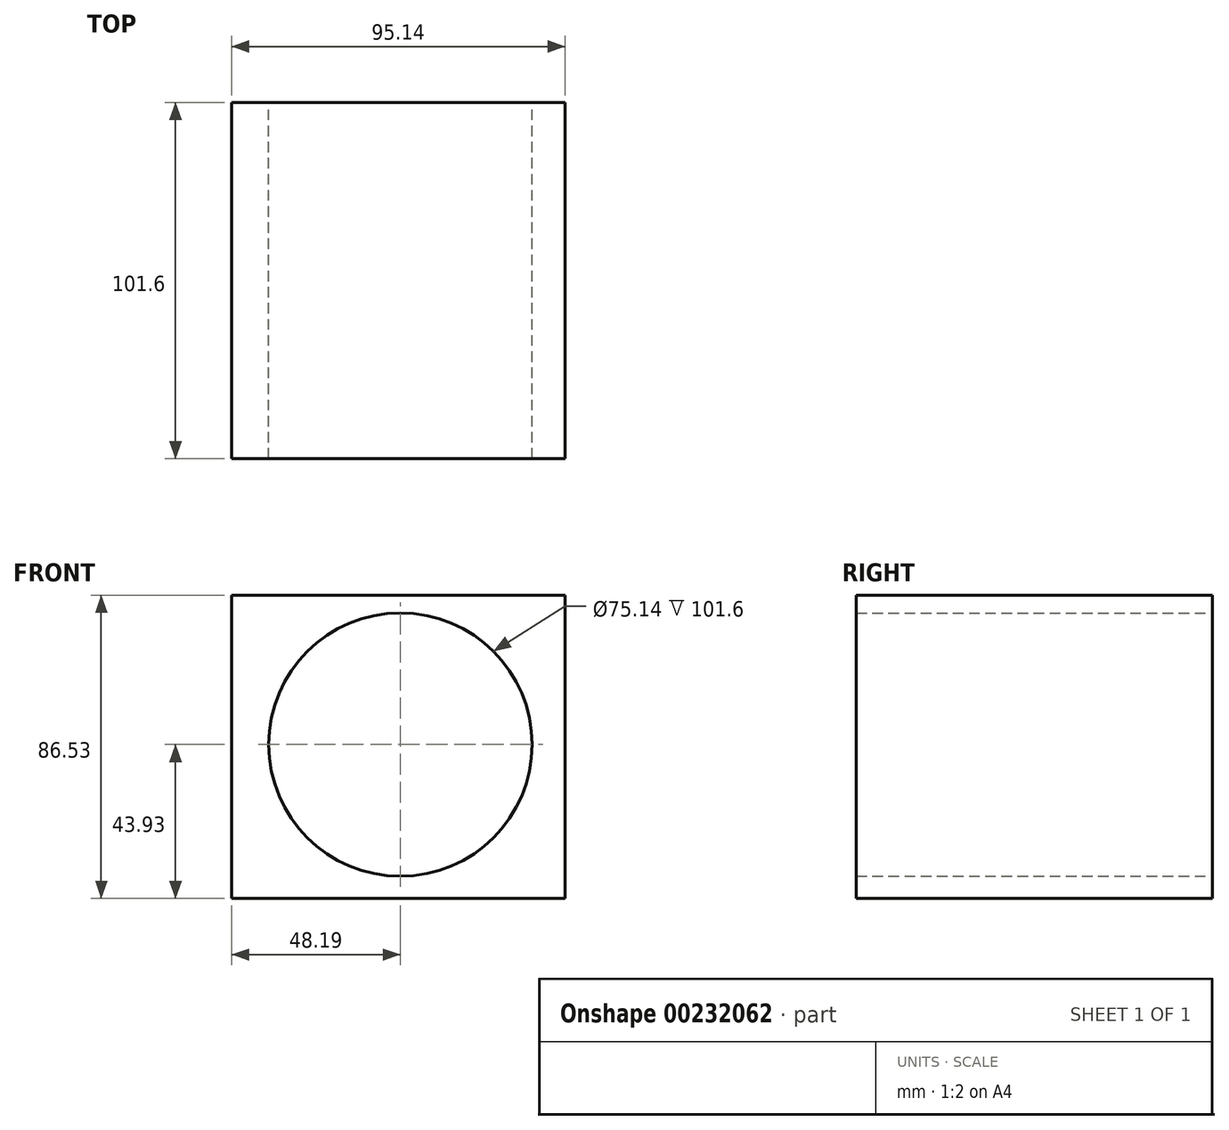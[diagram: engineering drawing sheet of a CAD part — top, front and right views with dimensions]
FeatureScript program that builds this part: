
annotation { "Feature Type Name" : "Feature", "Feature Type Description" : "" }
export const myFeature = defineFeature(function(context is Context, id is Id, definition is map)
    precondition{}
    {
        {
            var Q0;
            Q0=qCreatedBy(makeId("Front.planeOp"),FACE);
            var sketch = newSketch(context, id + "F0", { "sketchPlane" : qUnion([Q0])});
            skCircle(sketch, "E0", {"center": v(0, 0) * mm, "radius": 37.57 * mm});
            skLineSegment(sketch, "E1.bottom", {"start": v(-48.19, 42.6) * mm, "end": v(46.95, 42.6) * mm});
            skLineSegment(sketch, "E1.top", {"start": v(-48.19, -43.93) * mm, "end": v(46.95, -43.93) * mm});
            skLineSegment(sketch, "E1.left", {"start": v(-48.19, 42.6) * mm, "end": v(-48.19, -43.93) * mm});
            skLineSegment(sketch, "E1.right", {"start": v(46.95, 42.6) * mm, "end": v(46.95, -43.93) * mm});
            skSolve(sketch);
        }
        {
            var Q0;
            Q0=makeQuery(id+"F0.imprint","IMPRINT",FACE,{"disambiguationData":[TD([[makeQuery(id+"F0.imprint","IMPRINT",EDGE,{"derivedFrom":sQuery(id+"F0.wireOp",EDGE,"E0")}),-1.0]])]});
            extrude(context, id + "F1", {"entities" : qUnion([Q0]), "depth" : 101.6 * mm});
        }
    });
